# Revit family: Hager-Orion_Plus-IP66-D200-Cl.II-Poly_encl-630A-NoHosted-PT-pt
name_source: partatom
category: Electrical Equipment
units: mm (PartAtom-declared; Revit-internal decimal feet)

## family parameters
Always vertical = Yes
Cut with Voids When Loaded = No
Panel Configuration = Two Columns, Circuits Across
Part Type = Panelboard
Room Calculation Point = No
Round Connector Dimension = Use Diameter
Shared = No
Work Plane-Based = Yes

## types (6) — shared parameters
Default Elevation = 1219 mm
EF000003 - Método de montagem = EV000384 - Montagem em superfície (gesso)
EF000007 - Cor = EV000270 - Cinzento
EF000049 - Profundidade = 200 mm  [stored 0.656168 ft]
EF000116 - Número RAL = 7035
EF000118 - Com tampa de montagem = No
EF000339 - Tipo de difusor = EV004216 - Porta
EF001088 - Extensão possível = No
EF001131 - Profundidade interior = 200 mm  [stored 0.656168 ft]
EF001596 - Material do corpo = EV000139 - Plástico
EF003532 - Adequado para uso no exterior = Yes
EF004464 - Tipo de porta = EV002646 - Único
EF005474 - Grau de proteção (IP) = EV006422 - IP66
EF006306 - Com fecho = Yes
EF007800 - Adequado para proteção contra raios = No
EF008873 - Corrente nominal (In) = 630 A
EF009212 - Tipo de tampa = EV000116 - Fechado
EF015940 - Tampa com libertação de sobrepressão = No
HG000002 - Com porta ou tampa = Yes
HG000003 - Gama = Orion Plus
HG000006 - Encastrado = No
HG000009 - Porta dupla = No
HG000010 - Portas assimétricas = No
HG000023 - Recinto de secção dupla = No
HG000024 - Altura da secção inferior = 600 mm
HG000026 - Instalação no chão = No
Manufacturer = Hager
Type Comments = Orion Plus
zero-valued in all types: EF000218 - Profundidade incorporada, EF000437 - Número de entradas de condutores, EF009554 - Número de aberturas para placas de flange, HG000027 - Altura da Plinta

## per-type parameters (varying)
| type | EF000008 - Largura | EF000040 - Altura | EF000266 - Número de linhas | EF002950 - Largura em número de módulos | EF004293 - Força de impacto | EF004427 - Número de módulos | EF006244 - Tampa/porta transparente | EF009170 - Espessura do material do invólucro | EF009171 - Espessura do material da porta/tampa | HG000004 - Referência do Fabricante |
| Montagem em superfície (gesso) IP66 L300 A500 P200  - FL209B | 300 mm  [stored 0.984252 ft] | 500 mm  [stored 1.64042 ft] | 3 | 12 | EV008784 - IK10 | 36 | No | 2 mm  [stored 0.00656168 ft] | 2 mm  [stored 0.00656168 ft] | FL209B |
| Montagem em superfície (gesso) IP66 L300 A500 P200  - FL259B | 300 mm  [stored 0.984252 ft] | 500 mm  [stored 1.64042 ft] | 3 | 12 | EV006814 - IK08 | 36 | Yes | 3 mm  [stored 0.00984252 ft] | 3 mm  [stored 0.00984252 ft] | FL259B |
| Montagem em superfície (gesso) IP66 L400 A500 P200  - FL213B | 400 mm  [stored 1.31234 ft] | 500 mm  [stored 1.64042 ft] | 3 | 18 | EV008784 - IK10 | 54 | No | 2 mm  [stored 0.00656168 ft] | 2 mm  [stored 0.00656168 ft] | FL213B |
| Montagem em superfície (gesso) IP66 L400 A500 P200  - FL263B | 400 mm  [stored 1.31234 ft] | 500 mm  [stored 1.64042 ft] | 3 | 18 | EV006814 - IK08 | 54 | Yes | 3 mm  [stored 0.00984252 ft] | 3 mm  [stored 0.00984252 ft] | FL263B |
| Montagem em superfície (gesso) IP66 L400 A650 P200  - FL216B | 400 mm  [stored 1.31234 ft] | 650 mm  [stored 2.13255 ft] | 4 | 18 | EV008784 - IK10 | 72 | No | 2 mm  [stored 0.00656168 ft] | 2 mm  [stored 0.00656168 ft] | FL216B |
| Montagem em superfície (gesso) IP66 L400 A650 P200  - FL266B | 400 mm  [stored 1.31234 ft] | 650 mm  [stored 2.13255 ft] | 4 | 18 | EV006814 - IK08 | 72 | Yes | 3 mm  [stored 0.00984252 ft] | 3 mm  [stored 0.00984252 ft] | FL266B |

note: [stored X ft] marks values corroborated as IEEE doubles in the binary element streams (Revit-internal decimal feet)

## geometry (parser evidence)
native form markers: Blend x4, Sweep x6
no freeform markers — native parametric forms only
